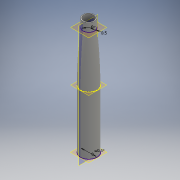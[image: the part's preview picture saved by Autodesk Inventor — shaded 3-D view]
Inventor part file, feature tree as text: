
AUTODESK INVENTOR PART (.ipt)
format: ipt  version: 2016 (Build 200138000, 138)  size: 129,024 bytes
history: native  units: mm
features: sketch x5, plane x3, revolve x1, extrude x1
ambient origin geometry x8: Origin, YZ Plane, XZ Plane, XY Plane, X Axis, Y Axis, Z Axis, Center Point
bodies: Body1 (feature_tree)
feature tree (10):
  sketch  "Sketch1"  dims[d0=9.0mm d1=0.5mm]
  plane  "Work Plane1"
  plane  "Work Plane2"
  sketch  "Sketch3"  dims[d5=6.0mm]
  sketch  "Sketch2"  dims[d2=35.0mm d3=65.0mm d4=0.5mm]
  plane  "Work Plane3"
  revolve  "Revolution2"  [1 undecoded]
  extrude  "Extrusion1"  Depth=65.0mm
  sketch  "Sketch4"  dims[d20=90.0deg]
  sketch  "Sketch5"  dims[d21=4.0mm d22=5.0mm d23=0.0mm]
note: 1 required parameter value undecoded (feature->parameter linkage not recoverable at this tier; creation-order binding heuristic only, values carry confidence <= 0.55)
